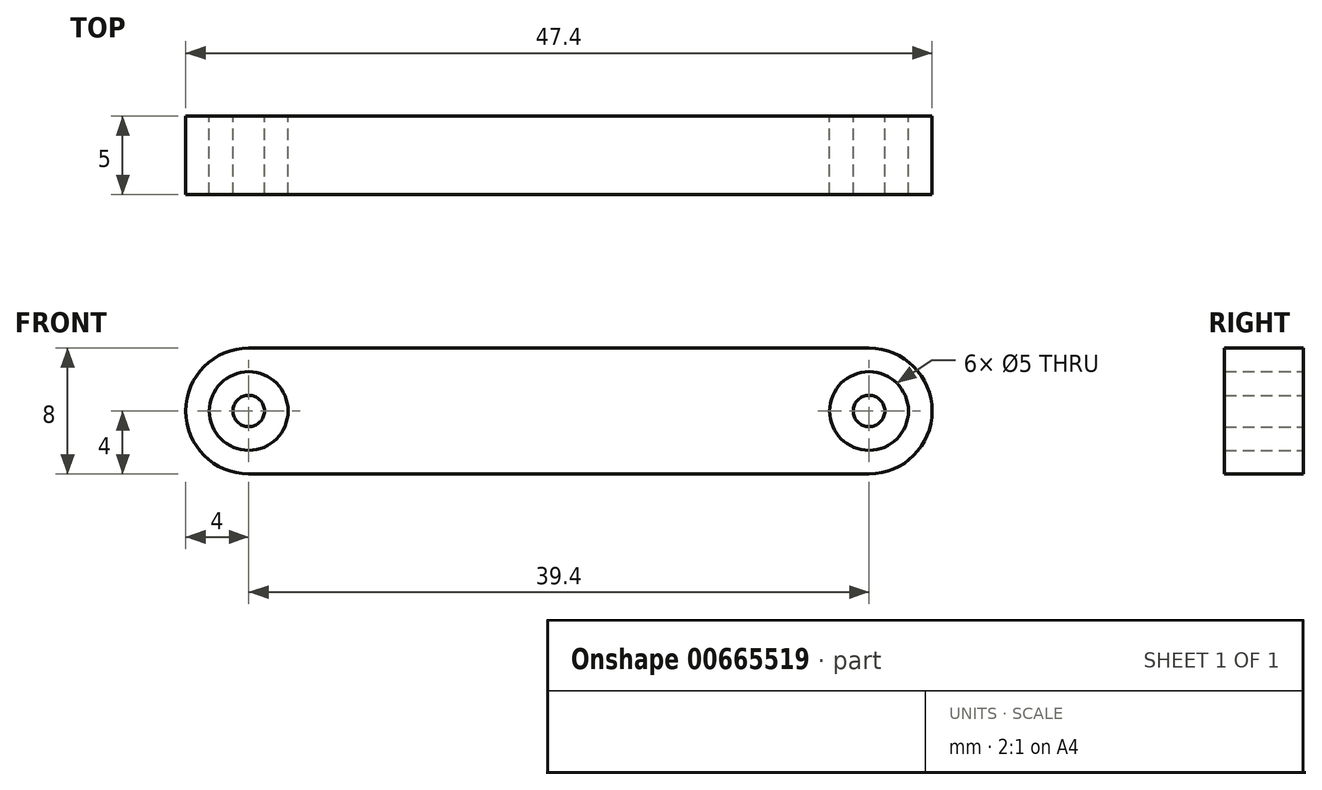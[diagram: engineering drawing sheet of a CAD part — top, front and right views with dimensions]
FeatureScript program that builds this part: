
annotation { "Feature Type Name" : "Feature", "Feature Type Description" : "" }
export const myFeature = defineFeature(function(context is Context, id is Id, definition is map)
    precondition{}
    {
        {
            var Q0;
            Q0=qCreatedBy(makeId("Front.planeOp"),FACE);
            var sketch = newSketch(context, id + "F0", { "sketchPlane" : qUnion([Q0])});
            skArc(sketch, "E0", {"start": v(0, 4) * mm, "mid": v(-4, 0) * mm, "end": v(0, -4) * mm});
            skArc(sketch, "E1", {"start": v(39.4, -4) * mm, "mid": v(43.4, 0) * mm, "end": v(39.4, 4) * mm});
            skLineSegment(sketch, "E2", {"start": v(0, 4) * mm, "end": v(39.4, 4) * mm});
            skLineSegment(sketch, "E3", {"start": v(0, -4) * mm, "end": v(39.4, -4) * mm});
            skCircle(sketch, "E4", {"center": v(0, 0) * mm, "radius": 2.5 * mm});
            skCircle(sketch, "E5", {"center": v(39.4, 0) * mm, "radius": 2.5 * mm});
            skCircle(sketch, "E6", {"center": v(0, 0) * mm, "radius": 1 * mm});
            skCircle(sketch, "E7", {"center": v(39.4, 0) * mm, "radius": 1 * mm});
            skSolve(sketch);
        }
        {
            var Q0;
            Q0 = qSketchRegion(id + "F0", true);
            var Q1;
            Q1=makeQuery(id+"F0.imprint","IMPRINT",FACE,{"disambiguationData":[TD([[makeQuery(id+"F0.imprint","IMPRINT",EDGE,{"derivedFrom":sQuery(id+"F0.wireOp",EDGE,"E6")}),1.0]])]});
            var Q2;
            Q2=makeQuery(id+"F0.imprint","IMPRINT",FACE,{"disambiguationData":[TD([[makeQuery(id+"F0.imprint","IMPRINT",EDGE,{"derivedFrom":sQuery(id+"F0.wireOp",EDGE,"E7")}),1.0]])]});
            extrude(context, id + "F1", {"entities" : qUnion([Q0, Q1, Q2]), "depth" : 5 * mm, "offsetDistance" : 25.4 * mm});
        }
    });
